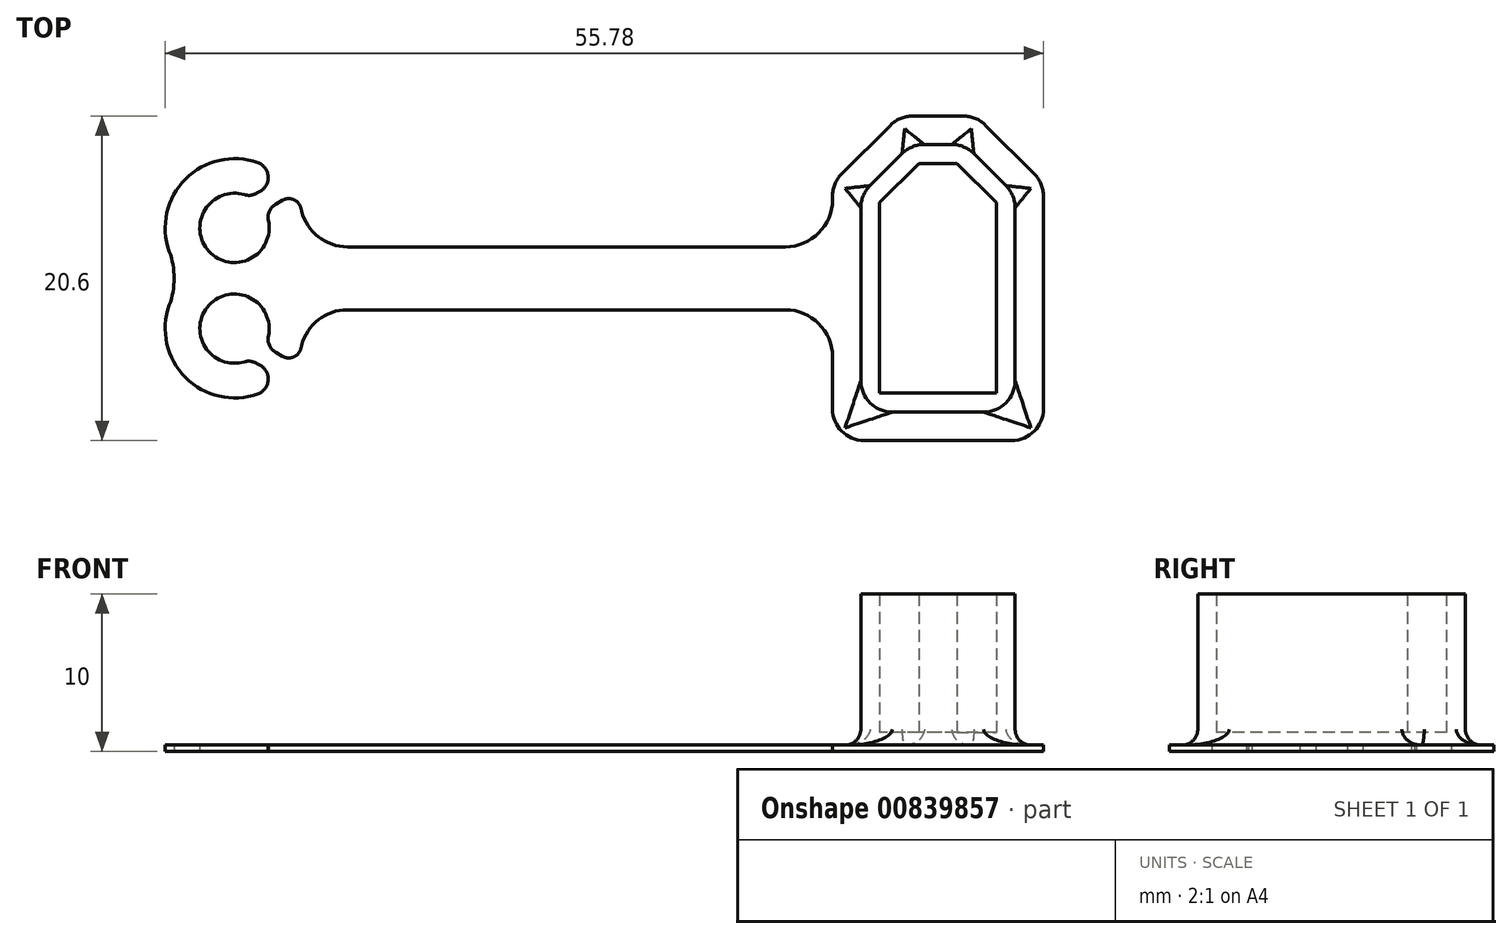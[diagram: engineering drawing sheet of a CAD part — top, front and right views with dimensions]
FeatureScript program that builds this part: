
annotation { "Feature Type Name" : "Feature", "Feature Type Description" : "" }
export const myFeature = defineFeature(function(context is Context, id is Id, definition is map)
    precondition{}
    {
        {
            var Q0;
            Q0=qCreatedBy(makeId("Top.planeOp"),FACE);
            var sketch = newSketch(context, id + "F0", { "sketchPlane" : qUnion([Q0])});
            skLineSegment(sketch, "E0.bottom", {"start": v(1.2, 7.3) * mm, "end": v(-1.2, 7.3) * mm});
            skLineSegment(sketch, "E0.top", {"start": v(3.7, -7.3) * mm, "end": v(-3.7, -7.3) * mm});
            skLineSegment(sketch, "E0.left", {"start": v(3.7, 4.8) * mm, "end": v(3.7, -7.3) * mm});
            skLineSegment(sketch, "E0.right", {"start": v(-3.7, 4.8) * mm, "end": v(-3.7, -7.3) * mm});
            skPoint(sketch, "E0.middle", {"position": v(0, 0) * mm});
            skLineSegment(sketch, "E1", {"start": v(0, 7.3) * mm, "end": v(0, 8.77) * mm, "construction": true});
            skLineSegment(sketch, "E2", {"start": v(-1.2, 7.3) * mm, "end": v(-3.7, 4.8) * mm});
            skLineSegment(sketch, "E3", {"start": v(1.2, 7.3) * mm, "end": v(3.7, 4.8) * mm});
            skPoint(sketch, "E4.orphan", {"position": v(-3.7, 7.3) * mm});
            skPoint(sketch, "E5.orphan", {"position": v(3.7, 7.3) * mm});
            skLineSegment(sketch, "E6.0", {"start": v(-1.7, 8.5) * mm, "end": v(-4.9, 5.3) * mm});
            skLineSegment(sketch, "E6.1", {"start": v(4.9, -8.5) * mm, "end": v(-4.9, -8.5) * mm});
            skLineSegment(sketch, "E6.2", {"start": v(4.9, 5.3) * mm, "end": v(4.9, -8.5) * mm});
            skLineSegment(sketch, "E6.3", {"start": v(-4.9, 5.3) * mm, "end": v(-4.9, -8.5) * mm});
            skLineSegment(sketch, "E6.4", {"start": v(1.7, 8.5) * mm, "end": v(4.9, 5.3) * mm});
            skLineSegment(sketch, "E6.5", {"start": v(1.7, 8.5) * mm, "end": v(-1.7, 8.5) * mm});
            skSolve(sketch);
        }
        {
            var Q0;
            Q0 = qSketchRegion(id + "F0", true);
            var Q1;
            Q1=makeQuery(id+"F0.imprint","IMPRINT",FACE,{"disambiguationData":[TD([[makeQuery(id+"F0.imprint","IMPRINT",EDGE,{"derivedFrom":sQuery(id+"F0.wireOp",EDGE,"E0.bottom")}),1.0]])]});
            extrude(context, id + "F1", {"entities" : qUnion([Q0, Q1]), "depth" : 10 * mm, "offsetDistance" : 25 * mm});
        }
        {
            var Q0;
            Q0=makeQuery(id+"F1.opExtrude","CAP_FACE",FACE,{"disambiguationData":[OSD([sQuery(id+"F0.wireOp",EDGE,"E6.0"),sQuery(id+"F0.wireOp",EDGE,"E6.1"),sQuery(id+"F0.wireOp",EDGE,"E6.2"),sQuery(id+"F0.wireOp",EDGE,"E6.3"),sQuery(id+"F0.wireOp",EDGE,"E6.4"),sQuery(id+"F0.wireOp",EDGE,"E6.5")])],"isStart":false});
            shell(context, id + "F2", {"entities" : qUnion([Q0]), "thickness" : 1.2 * mm});
        }
        {
            var Q0;
            Q0=qCreatedBy(makeId("Top.planeOp"),FACE);
            var sketch = newSketch(context, id + "F3", { "sketchPlane" : qUnion([Q0])});
            skLineSegment(sketch, "E7.0", {"start": v(-1.61, 10.3) * mm, "end": v(1.61, 10.3) * mm});
            skLineSegment(sketch, "E7.1", {"start": v(6.7, 5.21) * mm, "end": v(6.7, -8.3) * mm});
            skLineSegment(sketch, "E7.2", {"start": v(4.7, -10.3) * mm, "end": v(-4.7, -10.3) * mm});
            skLineSegment(sketch, "E7.3", {"start": v(3.03, 9.71) * mm, "end": v(6.11, 6.63) * mm});
            skLineSegment(sketch, "E7.4", {"start": v(-6.7, 5) * mm, "end": v(-6.7, 5.21) * mm});
            skLineSegment(sketch, "E7.5", {"start": v(-6.11, 6.63) * mm, "end": v(-3.03, 9.71) * mm});
            skLineSegment(sketch, "E8", {"start": v(-6.7, 0) * mm, "end": v(-22.7, 0) * mm});
            skArc(sketch, "E9", {"start": v(-44.05, 5.3) * mm, "mid": v(-46.3, 1.71) * mm, "end": v(-42.53, 3.65) * mm});
            skArc(sketch, "E10", {"start": v(-42.53, -3.65) * mm, "mid": v(-46.3, -1.71) * mm, "end": v(-44.05, -5.3) * mm});
            skArc(sketch, "E11.0", {"start": v(-40.41, 4.27) * mm, "mid": v(-40.44, 4.38) * mm, "end": v(-40.48, 4.5) * mm});
            skArc(sketch, "E12.0", {"start": v(-48.82, -1.7) * mm, "mid": v(-47.8, -6.3) * mm, "end": v(-43.2, -7.34) * mm});
            skPoint(sketch, "E13.visualSharp", {"position": v(-47.7, 0) * mm});
            skArc(sketch, "E13.filletArc", {"start": v(-48.82, -1.7) * mm, "mid": v(-48.52, 0) * mm, "end": v(-48.82, 1.7) * mm});
            skLineSegment(sketch, "E14.0", {"start": v(-9.7, 2) * mm, "end": v(-37.5, 2) * mm});
            skLineSegment(sketch, "E15.0", {"start": v(-9.7, -2) * mm, "end": v(-37.5, -2) * mm});
            skPoint(sketch, "E16.visualSharp", {"position": v(-40.45, 2) * mm});
            skArc(sketch, "E16.filletArc", {"start": v(-40.41, 4.27) * mm, "mid": v(-39.35, 2.63) * mm, "end": v(-37.5, 2) * mm});
            skPoint(sketch, "E17.visualSharp", {"position": v(-40.45, -2) * mm});
            skArc(sketch, "E17.filletArc", {"start": v(-37.5, -2) * mm, "mid": v(-39.35, -2.63) * mm, "end": v(-40.41, -4.27) * mm});
            skArc(sketch, "E18.filletArc", {"start": v(-9.7, 2) * mm, "mid": v(-7.58, 2.88) * mm, "end": v(-6.7, 5) * mm});
            skLineSegment(sketch, "E19", {"start": v(-6.7, -5) * mm, "end": v(-6.7, -8.3) * mm});
            skPoint(sketch, "E20.visualSharp", {"position": v(-6.7, -2) * mm});
            skArc(sketch, "E20.filletArc", {"start": v(-6.7, -5) * mm, "mid": v(-7.58, -2.88) * mm, "end": v(-9.7, -2) * mm});
            skPoint(sketch, "E21.visualSharp", {"position": v(-6.7, 6.04) * mm});
            skArc(sketch, "E21.filletArc", {"start": v(-6.11, 6.63) * mm, "mid": v(-6.55, 5.98) * mm, "end": v(-6.7, 5.21) * mm});
            skPoint(sketch, "E22.visualSharp", {"position": v(-2.44, 10.3) * mm});
            skArc(sketch, "E22.filletArc", {"start": v(-1.61, 10.3) * mm, "mid": v(-2.38, 10.15) * mm, "end": v(-3.03, 9.71) * mm});
            skPoint(sketch, "E23.visualSharp", {"position": v(2.44, 10.3) * mm});
            skArc(sketch, "E23.filletArc", {"start": v(3.03, 9.71) * mm, "mid": v(2.38, 10.15) * mm, "end": v(1.61, 10.3) * mm});
            skPoint(sketch, "E24.visualSharp", {"position": v(6.7, 6.04) * mm});
            skArc(sketch, "E24.filletArc", {"start": v(6.7, 5.21) * mm, "mid": v(6.55, 5.98) * mm, "end": v(6.11, 6.63) * mm});
            skPoint(sketch, "E25.visualSharp", {"position": v(6.7, -10.3) * mm});
            skArc(sketch, "E25.filletArc", {"start": v(4.7, -10.3) * mm, "mid": v(6.11, -9.71) * mm, "end": v(6.7, -8.3) * mm});
            skPoint(sketch, "E26.visualSharp", {"position": v(-6.7, -10.3) * mm});
            skArc(sketch, "E26.filletArc", {"start": v(-6.7, -8.3) * mm, "mid": v(-6.11, -9.71) * mm, "end": v(-4.7, -10.3) * mm});
            skLineSegment(sketch, "E27", {"start": v(-42.05, 4.72) * mm, "end": v(-41.64, 4.95) * mm});
            skLineSegment(sketch, "E28.0", {"start": v(-43.27, 5.4) * mm, "end": v(-43.04, 5.54) * mm});
            skLineSegment(sketch, "E29", {"start": v(-42.05, -4.72) * mm, "end": v(-41.64, -4.95) * mm});
            skLineSegment(sketch, "E30.0", {"start": v(-43.27, -5.4) * mm, "end": v(-43.04, -5.54) * mm});
            skArc(sketch, "E31.trimOffspring", {"start": v(-40.48, -4.5) * mm, "mid": v(-40.44, -4.38) * mm, "end": v(-40.41, -4.27) * mm});
            skArc(sketch, "E32.trimOffspring", {"start": v(-43.2, 7.34) * mm, "mid": v(-47.8, 6.3) * mm, "end": v(-48.82, 1.7) * mm});
            skPoint(sketch, "E33.visualSharp", {"position": v(-43.68, 5.16) * mm});
            skArc(sketch, "E33.filletArc", {"start": v(-44.05, 5.3) * mm, "mid": v(-43.65, 5.27) * mm, "end": v(-43.27, 5.4) * mm});
            skPoint(sketch, "E34.visualSharp", {"position": v(-41.61, 6.36) * mm});
            skArc(sketch, "E34.filletArc", {"start": v(-43.04, 5.54) * mm, "mid": v(-42.54, 6.5) * mm, "end": v(-43.2, 7.34) * mm});
            skPoint(sketch, "E35.visualSharp", {"position": v(-42.77, 4.3) * mm});
            skArc(sketch, "E35.filletArc", {"start": v(-42.05, 4.72) * mm, "mid": v(-42.46, 4.26) * mm, "end": v(-42.53, 3.65) * mm});
            skPoint(sketch, "E36.visualSharp", {"position": v(-40.87, 5.4) * mm});
            skArc(sketch, "E36.filletArc", {"start": v(-40.48, 4.5) * mm, "mid": v(-40.95, 5) * mm, "end": v(-41.64, 4.95) * mm});
            skPoint(sketch, "E37.visualSharp", {"position": v(-40.87, -5.4) * mm});
            skArc(sketch, "E37.filletArc", {"start": v(-41.64, -4.95) * mm, "mid": v(-40.95, -5) * mm, "end": v(-40.48, -4.5) * mm});
            skPoint(sketch, "E38.visualSharp", {"position": v(-42.77, -4.3) * mm});
            skArc(sketch, "E38.filletArc", {"start": v(-42.53, -3.65) * mm, "mid": v(-42.46, -4.26) * mm, "end": v(-42.05, -4.72) * mm});
            skPoint(sketch, "E39.visualSharp", {"position": v(-43.68, -5.16) * mm});
            skArc(sketch, "E39.filletArc", {"start": v(-43.27, -5.4) * mm, "mid": v(-43.65, -5.27) * mm, "end": v(-44.05, -5.3) * mm});
            skPoint(sketch, "E40.visualSharp", {"position": v(-41.61, -6.36) * mm});
            skArc(sketch, "E40.filletArc", {"start": v(-43.2, -7.34) * mm, "mid": v(-42.54, -6.5) * mm, "end": v(-43.04, -5.54) * mm});
            skSolve(sketch);
        }
        {
            var Q0;
            Q0=makeQuery(id+"F3.imprint","IMPRINT",FACE,{"disambiguationData":[TD([[makeQuery(id+"F3.imprint","IMPRINT",EDGE,{"derivedFrom":sQuery(id+"F3.wireOp",EDGE,"E7.0")}),-1.0]])]});
            extrude(context, id + "F4", {"entities" : qUnion([Q0]), "operationType" : NewBodyOperationType.ADD, "depth" : 0.4 * mm, "offsetDistance" : 25 * mm});
        }
        {
            var Q0;
            Q0=makeQuery(id+"F4.boolean.opBoolean","INTERSECT",EDGE,{"derivedFrom":[makeQuery(id+"F1.opExtrude","SWEPT_FACE",FACE,{"disambiguationData":[OSD([sQuery(id+"F0.wireOp",EDGE,"E6.1")])]}),makeQuery(id+"F4.opExtrude","CAP_FACE",FACE,{"disambiguationData":[OSD([sQuery(id+"F3.wireOp",EDGE,"E7.0"),sQuery(id+"F3.wireOp",EDGE,"E7.1"),sQuery(id+"F3.wireOp",EDGE,"E7.2"),sQuery(id+"F3.wireOp",EDGE,"E7.3"),sQuery(id+"F3.wireOp",EDGE,"E7.4"),sQuery(id+"F3.wireOp",EDGE,"E7.5"),sQuery(id+"F3.wireOp",EDGE,"E9"),sQuery(id+"F3.wireOp",EDGE,"E10"),sQuery(id+"F3.wireOp",EDGE,"E11.0"),sQuery(id+"F3.wireOp",EDGE,"E12.0"),sQuery(id+"F3.wireOp",EDGE,"E13.filletArc"),sQuery(id+"F3.wireOp",EDGE,"E14.0"),sQuery(id+"F3.wireOp",EDGE,"E15.0"),sQuery(id+"F3.wireOp",EDGE,"E16.filletArc"),sQuery(id+"F3.wireOp",EDGE,"E17.filletArc"),sQuery(id+"F3.wireOp",EDGE,"E18.filletArc"),sQuery(id+"F3.wireOp",EDGE,"E19"),sQuery(id+"F3.wireOp",EDGE,"E20.filletArc"),sQuery(id+"F3.wireOp",EDGE,"E21.filletArc"),sQuery(id+"F3.wireOp",EDGE,"E22.filletArc"),sQuery(id+"F3.wireOp",EDGE,"E23.filletArc"),sQuery(id+"F3.wireOp",EDGE,"E24.filletArc"),sQuery(id+"F3.wireOp",EDGE,"E25.filletArc"),sQuery(id+"F3.wireOp",EDGE,"E26.filletArc"),sQuery(id+"F3.wireOp",EDGE,"E27"),sQuery(id+"F3.wireOp",EDGE,"E28.0"),sQuery(id+"F3.wireOp",EDGE,"E29"),sQuery(id+"F3.wireOp",EDGE,"E30.0"),sQuery(id+"F3.wireOp",EDGE,"E31.trimOffspring"),sQuery(id+"F3.wireOp",EDGE,"E32.trimOffspring"),sQuery(id+"F3.wireOp",EDGE,"E33.filletArc"),sQuery(id+"F3.wireOp",EDGE,"E34.filletArc"),sQuery(id+"F3.wireOp",EDGE,"E35.filletArc"),sQuery(id+"F3.wireOp",EDGE,"E36.filletArc"),sQuery(id+"F3.wireOp",EDGE,"E37.filletArc"),sQuery(id+"F3.wireOp",EDGE,"E38.filletArc"),sQuery(id+"F3.wireOp",EDGE,"E39.filletArc"),sQuery(id+"F3.wireOp",EDGE,"E40.filletArc")])],"isStart":false})]});
            var Q1;
            Q1=makeQuery(id+"F4.boolean.opBoolean","INTERSECT",EDGE,{"derivedFrom":[makeQuery(id+"F1.opExtrude","SWEPT_FACE",FACE,{"disambiguationData":[OSD([sQuery(id+"F0.wireOp",EDGE,"E6.2")])]}),makeQuery(id+"F4.opExtrude","CAP_FACE",FACE,{"disambiguationData":[OSD([sQuery(id+"F3.wireOp",EDGE,"E7.0"),sQuery(id+"F3.wireOp",EDGE,"E7.1"),sQuery(id+"F3.wireOp",EDGE,"E7.2"),sQuery(id+"F3.wireOp",EDGE,"E7.3"),sQuery(id+"F3.wireOp",EDGE,"E7.4"),sQuery(id+"F3.wireOp",EDGE,"E7.5"),sQuery(id+"F3.wireOp",EDGE,"E9"),sQuery(id+"F3.wireOp",EDGE,"E10"),sQuery(id+"F3.wireOp",EDGE,"E11.0"),sQuery(id+"F3.wireOp",EDGE,"E12.0"),sQuery(id+"F3.wireOp",EDGE,"E13.filletArc"),sQuery(id+"F3.wireOp",EDGE,"E14.0"),sQuery(id+"F3.wireOp",EDGE,"E15.0"),sQuery(id+"F3.wireOp",EDGE,"E16.filletArc"),sQuery(id+"F3.wireOp",EDGE,"E17.filletArc"),sQuery(id+"F3.wireOp",EDGE,"E18.filletArc"),sQuery(id+"F3.wireOp",EDGE,"E19"),sQuery(id+"F3.wireOp",EDGE,"E20.filletArc"),sQuery(id+"F3.wireOp",EDGE,"E21.filletArc"),sQuery(id+"F3.wireOp",EDGE,"E22.filletArc"),sQuery(id+"F3.wireOp",EDGE,"E23.filletArc"),sQuery(id+"F3.wireOp",EDGE,"E24.filletArc"),sQuery(id+"F3.wireOp",EDGE,"E25.filletArc"),sQuery(id+"F3.wireOp",EDGE,"E26.filletArc"),sQuery(id+"F3.wireOp",EDGE,"E27"),sQuery(id+"F3.wireOp",EDGE,"E28.0"),sQuery(id+"F3.wireOp",EDGE,"E29"),sQuery(id+"F3.wireOp",EDGE,"E30.0"),sQuery(id+"F3.wireOp",EDGE,"E31.trimOffspring"),sQuery(id+"F3.wireOp",EDGE,"E32.trimOffspring"),sQuery(id+"F3.wireOp",EDGE,"E33.filletArc"),sQuery(id+"F3.wireOp",EDGE,"E34.filletArc"),sQuery(id+"F3.wireOp",EDGE,"E35.filletArc"),sQuery(id+"F3.wireOp",EDGE,"E36.filletArc"),sQuery(id+"F3.wireOp",EDGE,"E37.filletArc"),sQuery(id+"F3.wireOp",EDGE,"E38.filletArc"),sQuery(id+"F3.wireOp",EDGE,"E39.filletArc"),sQuery(id+"F3.wireOp",EDGE,"E40.filletArc")])],"isStart":false})]});
            var Q2;
            Q2=makeQuery(id+"F4.boolean.opBoolean","INTERSECT",EDGE,{"derivedFrom":[makeQuery(id+"F1.opExtrude","SWEPT_FACE",FACE,{"disambiguationData":[OSD([sQuery(id+"F0.wireOp",EDGE,"E6.4")])]}),makeQuery(id+"F4.opExtrude","CAP_FACE",FACE,{"disambiguationData":[OSD([sQuery(id+"F3.wireOp",EDGE,"E7.0"),sQuery(id+"F3.wireOp",EDGE,"E7.1"),sQuery(id+"F3.wireOp",EDGE,"E7.2"),sQuery(id+"F3.wireOp",EDGE,"E7.3"),sQuery(id+"F3.wireOp",EDGE,"E7.4"),sQuery(id+"F3.wireOp",EDGE,"E7.5"),sQuery(id+"F3.wireOp",EDGE,"E9"),sQuery(id+"F3.wireOp",EDGE,"E10"),sQuery(id+"F3.wireOp",EDGE,"E11.0"),sQuery(id+"F3.wireOp",EDGE,"E12.0"),sQuery(id+"F3.wireOp",EDGE,"E13.filletArc"),sQuery(id+"F3.wireOp",EDGE,"E14.0"),sQuery(id+"F3.wireOp",EDGE,"E15.0"),sQuery(id+"F3.wireOp",EDGE,"E16.filletArc"),sQuery(id+"F3.wireOp",EDGE,"E17.filletArc"),sQuery(id+"F3.wireOp",EDGE,"E18.filletArc"),sQuery(id+"F3.wireOp",EDGE,"E19"),sQuery(id+"F3.wireOp",EDGE,"E20.filletArc"),sQuery(id+"F3.wireOp",EDGE,"E21.filletArc"),sQuery(id+"F3.wireOp",EDGE,"E22.filletArc"),sQuery(id+"F3.wireOp",EDGE,"E23.filletArc"),sQuery(id+"F3.wireOp",EDGE,"E24.filletArc"),sQuery(id+"F3.wireOp",EDGE,"E25.filletArc"),sQuery(id+"F3.wireOp",EDGE,"E26.filletArc"),sQuery(id+"F3.wireOp",EDGE,"E27"),sQuery(id+"F3.wireOp",EDGE,"E28.0"),sQuery(id+"F3.wireOp",EDGE,"E29"),sQuery(id+"F3.wireOp",EDGE,"E30.0"),sQuery(id+"F3.wireOp",EDGE,"E31.trimOffspring"),sQuery(id+"F3.wireOp",EDGE,"E32.trimOffspring"),sQuery(id+"F3.wireOp",EDGE,"E33.filletArc"),sQuery(id+"F3.wireOp",EDGE,"E34.filletArc"),sQuery(id+"F3.wireOp",EDGE,"E35.filletArc"),sQuery(id+"F3.wireOp",EDGE,"E36.filletArc"),sQuery(id+"F3.wireOp",EDGE,"E37.filletArc"),sQuery(id+"F3.wireOp",EDGE,"E38.filletArc"),sQuery(id+"F3.wireOp",EDGE,"E39.filletArc"),sQuery(id+"F3.wireOp",EDGE,"E40.filletArc")])],"isStart":false})]});
            var Q3;
            Q3=makeQuery(id+"F4.boolean.opBoolean","INTERSECT",EDGE,{"derivedFrom":[makeQuery(id+"F1.opExtrude","SWEPT_FACE",FACE,{"disambiguationData":[OSD([sQuery(id+"F0.wireOp",EDGE,"E6.5")])]}),makeQuery(id+"F4.opExtrude","CAP_FACE",FACE,{"disambiguationData":[OSD([sQuery(id+"F3.wireOp",EDGE,"E7.0"),sQuery(id+"F3.wireOp",EDGE,"E7.1"),sQuery(id+"F3.wireOp",EDGE,"E7.2"),sQuery(id+"F3.wireOp",EDGE,"E7.3"),sQuery(id+"F3.wireOp",EDGE,"E7.4"),sQuery(id+"F3.wireOp",EDGE,"E7.5"),sQuery(id+"F3.wireOp",EDGE,"E9"),sQuery(id+"F3.wireOp",EDGE,"E10"),sQuery(id+"F3.wireOp",EDGE,"E11.0"),sQuery(id+"F3.wireOp",EDGE,"E12.0"),sQuery(id+"F3.wireOp",EDGE,"E13.filletArc"),sQuery(id+"F3.wireOp",EDGE,"E14.0"),sQuery(id+"F3.wireOp",EDGE,"E15.0"),sQuery(id+"F3.wireOp",EDGE,"E16.filletArc"),sQuery(id+"F3.wireOp",EDGE,"E17.filletArc"),sQuery(id+"F3.wireOp",EDGE,"E18.filletArc"),sQuery(id+"F3.wireOp",EDGE,"E19"),sQuery(id+"F3.wireOp",EDGE,"E20.filletArc"),sQuery(id+"F3.wireOp",EDGE,"E21.filletArc"),sQuery(id+"F3.wireOp",EDGE,"E22.filletArc"),sQuery(id+"F3.wireOp",EDGE,"E23.filletArc"),sQuery(id+"F3.wireOp",EDGE,"E24.filletArc"),sQuery(id+"F3.wireOp",EDGE,"E25.filletArc"),sQuery(id+"F3.wireOp",EDGE,"E26.filletArc"),sQuery(id+"F3.wireOp",EDGE,"E27"),sQuery(id+"F3.wireOp",EDGE,"E28.0"),sQuery(id+"F3.wireOp",EDGE,"E29"),sQuery(id+"F3.wireOp",EDGE,"E30.0"),sQuery(id+"F3.wireOp",EDGE,"E31.trimOffspring"),sQuery(id+"F3.wireOp",EDGE,"E32.trimOffspring"),sQuery(id+"F3.wireOp",EDGE,"E33.filletArc"),sQuery(id+"F3.wireOp",EDGE,"E34.filletArc"),sQuery(id+"F3.wireOp",EDGE,"E35.filletArc"),sQuery(id+"F3.wireOp",EDGE,"E36.filletArc"),sQuery(id+"F3.wireOp",EDGE,"E37.filletArc"),sQuery(id+"F3.wireOp",EDGE,"E38.filletArc"),sQuery(id+"F3.wireOp",EDGE,"E39.filletArc"),sQuery(id+"F3.wireOp",EDGE,"E40.filletArc")])],"isStart":false})]});
            var Q4;
            Q4=makeQuery(id+"F4.boolean.opBoolean","INTERSECT",EDGE,{"derivedFrom":[makeQuery(id+"F1.opExtrude","SWEPT_FACE",FACE,{"disambiguationData":[OSD([sQuery(id+"F0.wireOp",EDGE,"E6.0")])]}),makeQuery(id+"F4.opExtrude","CAP_FACE",FACE,{"disambiguationData":[OSD([sQuery(id+"F3.wireOp",EDGE,"E7.0"),sQuery(id+"F3.wireOp",EDGE,"E7.1"),sQuery(id+"F3.wireOp",EDGE,"E7.2"),sQuery(id+"F3.wireOp",EDGE,"E7.3"),sQuery(id+"F3.wireOp",EDGE,"E7.4"),sQuery(id+"F3.wireOp",EDGE,"E7.5"),sQuery(id+"F3.wireOp",EDGE,"E9"),sQuery(id+"F3.wireOp",EDGE,"E10"),sQuery(id+"F3.wireOp",EDGE,"E11.0"),sQuery(id+"F3.wireOp",EDGE,"E12.0"),sQuery(id+"F3.wireOp",EDGE,"E13.filletArc"),sQuery(id+"F3.wireOp",EDGE,"E14.0"),sQuery(id+"F3.wireOp",EDGE,"E15.0"),sQuery(id+"F3.wireOp",EDGE,"E16.filletArc"),sQuery(id+"F3.wireOp",EDGE,"E17.filletArc"),sQuery(id+"F3.wireOp",EDGE,"E18.filletArc"),sQuery(id+"F3.wireOp",EDGE,"E19"),sQuery(id+"F3.wireOp",EDGE,"E20.filletArc"),sQuery(id+"F3.wireOp",EDGE,"E21.filletArc"),sQuery(id+"F3.wireOp",EDGE,"E22.filletArc"),sQuery(id+"F3.wireOp",EDGE,"E23.filletArc"),sQuery(id+"F3.wireOp",EDGE,"E24.filletArc"),sQuery(id+"F3.wireOp",EDGE,"E25.filletArc"),sQuery(id+"F3.wireOp",EDGE,"E26.filletArc"),sQuery(id+"F3.wireOp",EDGE,"E27"),sQuery(id+"F3.wireOp",EDGE,"E28.0"),sQuery(id+"F3.wireOp",EDGE,"E29"),sQuery(id+"F3.wireOp",EDGE,"E30.0"),sQuery(id+"F3.wireOp",EDGE,"E31.trimOffspring"),sQuery(id+"F3.wireOp",EDGE,"E32.trimOffspring"),sQuery(id+"F3.wireOp",EDGE,"E33.filletArc"),sQuery(id+"F3.wireOp",EDGE,"E34.filletArc"),sQuery(id+"F3.wireOp",EDGE,"E35.filletArc"),sQuery(id+"F3.wireOp",EDGE,"E36.filletArc"),sQuery(id+"F3.wireOp",EDGE,"E37.filletArc"),sQuery(id+"F3.wireOp",EDGE,"E38.filletArc"),sQuery(id+"F3.wireOp",EDGE,"E39.filletArc"),sQuery(id+"F3.wireOp",EDGE,"E40.filletArc")])],"isStart":false})]});
            var Q5;
            Q5=makeQuery(id+"F4.boolean.opBoolean","INTERSECT",EDGE,{"derivedFrom":[makeQuery(id+"F1.opExtrude","SWEPT_FACE",FACE,{"disambiguationData":[OSD([sQuery(id+"F0.wireOp",EDGE,"E6.3")])]}),makeQuery(id+"F4.opExtrude","CAP_FACE",FACE,{"disambiguationData":[OSD([sQuery(id+"F3.wireOp",EDGE,"E7.0"),sQuery(id+"F3.wireOp",EDGE,"E7.1"),sQuery(id+"F3.wireOp",EDGE,"E7.2"),sQuery(id+"F3.wireOp",EDGE,"E7.3"),sQuery(id+"F3.wireOp",EDGE,"E7.4"),sQuery(id+"F3.wireOp",EDGE,"E7.5"),sQuery(id+"F3.wireOp",EDGE,"E9"),sQuery(id+"F3.wireOp",EDGE,"E10"),sQuery(id+"F3.wireOp",EDGE,"E11.0"),sQuery(id+"F3.wireOp",EDGE,"E12.0"),sQuery(id+"F3.wireOp",EDGE,"E13.filletArc"),sQuery(id+"F3.wireOp",EDGE,"E14.0"),sQuery(id+"F3.wireOp",EDGE,"E15.0"),sQuery(id+"F3.wireOp",EDGE,"E16.filletArc"),sQuery(id+"F3.wireOp",EDGE,"E17.filletArc"),sQuery(id+"F3.wireOp",EDGE,"E18.filletArc"),sQuery(id+"F3.wireOp",EDGE,"E19"),sQuery(id+"F3.wireOp",EDGE,"E20.filletArc"),sQuery(id+"F3.wireOp",EDGE,"E21.filletArc"),sQuery(id+"F3.wireOp",EDGE,"E22.filletArc"),sQuery(id+"F3.wireOp",EDGE,"E23.filletArc"),sQuery(id+"F3.wireOp",EDGE,"E24.filletArc"),sQuery(id+"F3.wireOp",EDGE,"E25.filletArc"),sQuery(id+"F3.wireOp",EDGE,"E26.filletArc"),sQuery(id+"F3.wireOp",EDGE,"E27"),sQuery(id+"F3.wireOp",EDGE,"E28.0"),sQuery(id+"F3.wireOp",EDGE,"E29"),sQuery(id+"F3.wireOp",EDGE,"E30.0"),sQuery(id+"F3.wireOp",EDGE,"E31.trimOffspring"),sQuery(id+"F3.wireOp",EDGE,"E32.trimOffspring"),sQuery(id+"F3.wireOp",EDGE,"E33.filletArc"),sQuery(id+"F3.wireOp",EDGE,"E34.filletArc"),sQuery(id+"F3.wireOp",EDGE,"E35.filletArc"),sQuery(id+"F3.wireOp",EDGE,"E36.filletArc"),sQuery(id+"F3.wireOp",EDGE,"E37.filletArc"),sQuery(id+"F3.wireOp",EDGE,"E38.filletArc"),sQuery(id+"F3.wireOp",EDGE,"E39.filletArc"),sQuery(id+"F3.wireOp",EDGE,"E40.filletArc")])],"isStart":false})]});
            fillet(context, id + "F5", {"entities" : qUnion([Q0, Q1, Q2, Q3, Q4, Q5]), "radius" : 1 * mm, "tangentPropagation" : true, "allowEdgeOverflow" : false});
        }
        {
            var Q0;
            Q0=makeQuery(id+"F1.opExtrude","SWEPT_EDGE",EDGE,{"disambiguationData":[OSD([sQuery(id+"F0.wireOp",EDGE,"E6.1"),sQuery(id+"F0.wireOp",EDGE,"E6.2")])]});
            var Q1;
            Q1=makeQuery(id+"F1.opExtrude","SWEPT_EDGE",EDGE,{"disambiguationData":[OSD([sQuery(id+"F0.wireOp",EDGE,"E6.2"),sQuery(id+"F0.wireOp",EDGE,"E6.4")])]});
            var Q2;
            Q2=makeQuery(id+"F1.opExtrude","SWEPT_EDGE",EDGE,{"disambiguationData":[OSD([sQuery(id+"F0.wireOp",EDGE,"E6.4"),sQuery(id+"F0.wireOp",EDGE,"E6.5")])]});
            var Q3;
            Q3=makeQuery(id+"F1.opExtrude","SWEPT_EDGE",EDGE,{"disambiguationData":[OSD([sQuery(id+"F0.wireOp",EDGE,"E6.0"),sQuery(id+"F0.wireOp",EDGE,"E6.5")])]});
            var Q4;
            Q4=makeQuery(id+"F1.opExtrude","SWEPT_EDGE",EDGE,{"disambiguationData":[OSD([sQuery(id+"F0.wireOp",EDGE,"E6.0"),sQuery(id+"F0.wireOp",EDGE,"E6.3")])]});
            var Q5;
            Q5=makeQuery(id+"F1.opExtrude","SWEPT_EDGE",EDGE,{"disambiguationData":[OSD([sQuery(id+"F0.wireOp",EDGE,"E6.1"),sQuery(id+"F0.wireOp",EDGE,"E6.3")])]});
            fillet(context, id + "F6", {"entities" : qUnion([Q0, Q1, Q2, Q3, Q4, Q5]), "radius" : 2 * mm, "tangentPropagation" : true, "allowEdgeOverflow" : false});
        }
    });
